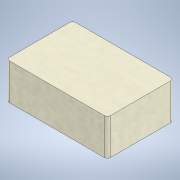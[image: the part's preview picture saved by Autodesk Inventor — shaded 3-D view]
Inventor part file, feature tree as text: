
AUTODESK INVENTOR PART (.ipt)
format: ipt  version: 2021 (Build 250183000, 183)  size: 125,440 bytes
history: native  units: mm
features: extrude x1, sketch x1
ambient origin geometry x8: Origin, YZ Plane, XZ Plane, XY Plane, X Axis, Y Axis, Z Axis, Center Point
bodies: Solid1 (feature_tree)
feature tree (2):
  extrude  "Extrusion1"  Depth=42.0mm
  sketch  "Sketch1"  dims[d0=64.0mm d1=42.0mm d2=2.0mm d3=23.0mm d4=0.0mm]
